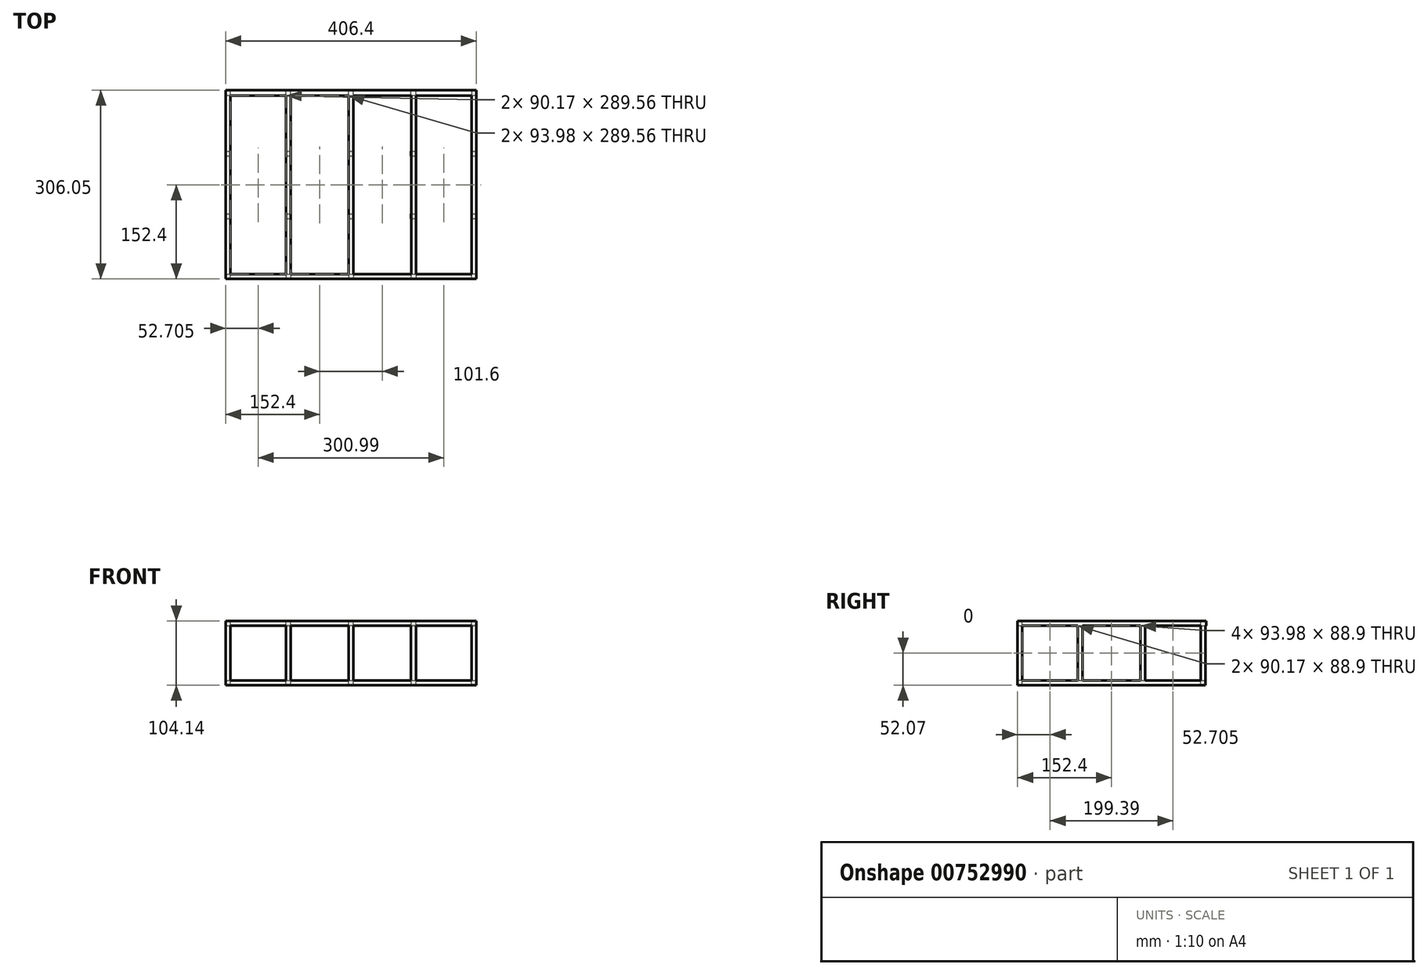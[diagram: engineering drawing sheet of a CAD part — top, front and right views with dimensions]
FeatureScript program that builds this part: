
annotation { "Feature Type Name" : "Feature", "Feature Type Description" : "" }
export const myFeature = defineFeature(function(context is Context, id is Id, definition is map)
    precondition{}
    {
        {
            var Q0;
            Q0=qCreatedBy(makeId("Top.planeOp"),FACE);
            var sketch = newSketch(context, id + "F0", { "sketchPlane" : qUnion([Q0])});
            skLineSegment(sketch, "E0.bottom", {"start": v(0, 0) * mm, "end": v(-406.4, 0) * mm});
            skLineSegment(sketch, "E0.top", {"start": v(0, 304.8) * mm, "end": v(-406.4, 304.8) * mm});
            skLineSegment(sketch, "E0.left", {"start": v(0, 0) * mm, "end": v(0, 304.8) * mm});
            skLineSegment(sketch, "E0.right", {"start": v(-406.4, 0) * mm, "end": v(-406.4, 304.8) * mm});
            skSolve(sketch);
        }
        {
            var Q0;
            Q0 = qSketchRegion(id + "F0", true);
            extrude(context, id + "F1", {"entities" : qUnion([Q0]), "depth" : 7.62 * mm, "offsetDistance" : 25.4 * mm});
        }
        {
            var Q0;
            Q0=makeQuery(id+"F1.opExtrude","CAP_FACE",FACE,{"disambiguationData":[OSD([sQuery(id+"F0.wireOp",EDGE,"E0.bottom"),sQuery(id+"F0.wireOp",EDGE,"E0.top"),sQuery(id+"F0.wireOp",EDGE,"E0.left"),sQuery(id+"F0.wireOp",EDGE,"E0.right")])],"isStart":false});
            var sketch = newSketch(context, id + "F2", { "sketchPlane" : qUnion([Q0])});
            skLineSegment(sketch, "E1", {"start": v(-406.4, 0) * mm, "end": v(-398.78, 0) * mm});
            skLineSegment(sketch, "E2", {"start": v(-398.78, 0) * mm, "end": v(-308.61, 0) * mm});
            skLineSegment(sketch, "E3", {"start": v(-308.61, 0) * mm, "end": v(-301, 0) * mm});
            skLineSegment(sketch, "E4", {"start": v(-105.41, 0) * mm, "end": v(-97.8, 0) * mm});
            skLineSegment(sketch, "E5", {"start": v(-97.8, 0) * mm, "end": v(-7.62, 0) * mm});
            skLineSegment(sketch, "E6", {"start": v(-7.62, 0) * mm, "end": v(-7.62, 7.62) * mm});
            skLineSegment(sketch, "E7", {"start": v(-406.4, 0) * mm, "end": v(-406.4, 297.18) * mm});
            skLineSegment(sketch, "E8.bottom", {"start": v(-7.62, 7.62) * mm, "end": v(-97.8, 7.62) * mm});
            skLineSegment(sketch, "E8.top", {"start": v(-7.62, 297.18) * mm, "end": v(-97.8, 297.18) * mm});
            skLineSegment(sketch, "E8.left", {"start": v(-7.62, 7.62) * mm, "end": v(-7.62, 297.18) * mm});
            skLineSegment(sketch, "E8.right", {"start": v(-97.8, 7.62) * mm, "end": v(-97.8, 297.18) * mm});
            skLineSegment(sketch, "E9.bottom", {"start": v(-398.78, 7.62) * mm, "end": v(-308.61, 7.62) * mm});
            skLineSegment(sketch, "E9.top", {"start": v(-398.78, 297.18) * mm, "end": v(-308.61, 297.18) * mm});
            skLineSegment(sketch, "E9.left", {"start": v(-398.78, 7.62) * mm, "end": v(-398.78, 297.18) * mm});
            skLineSegment(sketch, "E9.right", {"start": v(-308.61, 7.62) * mm, "end": v(-308.61, 297.18) * mm});
            skLineSegment(sketch, "E10", {"start": v(-105.41, 0) * mm, "end": v(-199.4, 0) * mm});
            skLineSegment(sketch, "E11", {"start": v(-199.4, 0) * mm, "end": v(-207.01, 0) * mm});
            skLineSegment(sketch, "E12", {"start": v(-207.01, 0) * mm, "end": v(-301, 0) * mm});
            skLineSegment(sketch, "E13.bottom", {"start": v(-301, 7.62) * mm, "end": v(-207.01, 7.62) * mm});
            skLineSegment(sketch, "E13.top", {"start": v(-301, 297.18) * mm, "end": v(-207.01, 297.18) * mm});
            skLineSegment(sketch, "E13.left", {"start": v(-301, 7.62) * mm, "end": v(-301, 297.18) * mm});
            skLineSegment(sketch, "E13.right", {"start": v(-207.01, 7.62) * mm, "end": v(-207.01, 297.18) * mm});
            skLineSegment(sketch, "E14.bottom", {"start": v(-199.4, 7.62) * mm, "end": v(-105.41, 7.62) * mm});
            skLineSegment(sketch, "E14.top", {"start": v(-199.4, 297.18) * mm, "end": v(-105.41, 297.18) * mm});
            skLineSegment(sketch, "E14.left", {"start": v(-199.4, 7.62) * mm, "end": v(-199.4, 297.18) * mm});
            skLineSegment(sketch, "E14.right", {"start": v(-105.41, 7.62) * mm, "end": v(-105.41, 297.18) * mm});
            skSolve(sketch);
        }
        {
            var Q0;
            Q0 = qSketchRegion(id + "F2", true);
            extrude(context, id + "F3", {"entities" : qUnion([Q0]), "operationType" : NewBodyOperationType.REMOVE, "oppositeDirection" : true, "depth" : 7.62 * mm, "offsetDistance" : 25.4 * mm});
        }
        {
            var Q0;
            Q0=makeQuery(id+"F1.opExtrude","CAP_FACE",FACE,{"disambiguationData":[OSD([sQuery(id+"F0.wireOp",EDGE,"E0.bottom"),sQuery(id+"F0.wireOp",EDGE,"E0.top"),sQuery(id+"F0.wireOp",EDGE,"E0.left"),sQuery(id+"F0.wireOp",EDGE,"E0.right")])],"isStart":false});
            var sketch = newSketch(context, id + "F4", { "sketchPlane" : qUnion([Q0])});
            skLineSegment(sketch, "E15.bottom", {"start": v(-406.4, 0) * mm, "end": v(-398.78, 0) * mm});
            skLineSegment(sketch, "E15.top", {"start": v(-406.4, 7.62) * mm, "end": v(-398.78, 7.62) * mm});
            skLineSegment(sketch, "E15.left", {"start": v(-406.4, 0) * mm, "end": v(-406.4, 7.62) * mm});
            skLineSegment(sketch, "E15.right", {"start": v(-398.78, 0) * mm, "end": v(-398.78, 7.62) * mm});
            skLineSegment(sketch, "E16.bottom", {"start": v(-308.61, 7.62) * mm, "end": v(-300.99, 7.62) * mm});
            skLineSegment(sketch, "E16.top", {"start": v(-308.61, 0) * mm, "end": v(-300.99, 0) * mm});
            skLineSegment(sketch, "E16.left", {"start": v(-308.61, 7.62) * mm, "end": v(-308.61, 0) * mm});
            skLineSegment(sketch, "E16.right", {"start": v(-300.99, 7.62) * mm, "end": v(-300.99, 0) * mm});
            skLineSegment(sketch, "E17.bottom", {"start": v(-105.74, 7.62) * mm, "end": v(-97.8, 7.62) * mm});
            skLineSegment(sketch, "E17.top", {"start": v(-105.74, 0) * mm, "end": v(-97.8, 0) * mm});
            skLineSegment(sketch, "E17.left", {"start": v(-105.74, 7.62) * mm, "end": v(-105.74, 0) * mm});
            skLineSegment(sketch, "E17.right", {"start": v(-97.8, 7.62) * mm, "end": v(-97.8, 0) * mm});
            skLineSegment(sketch, "E18.bottom", {"start": v(0, 0) * mm, "end": v(-7.62, 0) * mm});
            skLineSegment(sketch, "E18.top", {"start": v(0, 7.62) * mm, "end": v(-7.62, 7.62) * mm});
            skLineSegment(sketch, "E18.left", {"start": v(0, 0) * mm, "end": v(0, 7.62) * mm});
            skLineSegment(sketch, "E18.right", {"start": v(-7.62, 0) * mm, "end": v(-7.62, 7.62) * mm});
            skLineSegment(sketch, "E19.bottom", {"start": v(0, 304.8) * mm, "end": v(-7.62, 304.8) * mm});
            skLineSegment(sketch, "E19.top", {"start": v(0, 297.18) * mm, "end": v(-7.62, 297.18) * mm});
            skLineSegment(sketch, "E19.left", {"start": v(0, 304.8) * mm, "end": v(0, 297.18) * mm});
            skLineSegment(sketch, "E19.right", {"start": v(-7.62, 304.8) * mm, "end": v(-7.62, 297.18) * mm});
            skLineSegment(sketch, "E20.bottom", {"start": v(-97.8, 297.18) * mm, "end": v(-105.74, 297.18) * mm});
            skLineSegment(sketch, "E20.top", {"start": v(-97.8, 304.8) * mm, "end": v(-105.74, 304.8) * mm});
            skLineSegment(sketch, "E20.left", {"start": v(-97.8, 297.18) * mm, "end": v(-97.8, 304.8) * mm});
            skLineSegment(sketch, "E20.right", {"start": v(-105.74, 297.18) * mm, "end": v(-105.74, 304.8) * mm});
            skLineSegment(sketch, "E21.bottom", {"start": v(-301, 297.18) * mm, "end": v(-308.61, 297.18) * mm});
            skLineSegment(sketch, "E21.top", {"start": v(-301, 304.8) * mm, "end": v(-308.61, 304.8) * mm});
            skLineSegment(sketch, "E21.left", {"start": v(-301, 297.18) * mm, "end": v(-301, 304.8) * mm});
            skLineSegment(sketch, "E21.right", {"start": v(-308.61, 297.18) * mm, "end": v(-308.61, 304.8) * mm});
            skLineSegment(sketch, "E22.bottom", {"start": v(-398.78, 297.18) * mm, "end": v(-406.4, 297.18) * mm});
            skLineSegment(sketch, "E22.top", {"start": v(-398.78, 304.8) * mm, "end": v(-406.4, 304.8) * mm});
            skLineSegment(sketch, "E22.left", {"start": v(-398.78, 297.18) * mm, "end": v(-398.78, 304.8) * mm});
            skLineSegment(sketch, "E22.right", {"start": v(-406.4, 297.18) * mm, "end": v(-406.4, 304.8) * mm});
            skLineSegment(sketch, "E23", {"start": v(-406.4, 7.62) * mm, "end": v(-406.4, 97.8) * mm});
            skLineSegment(sketch, "E24", {"start": v(-406.4, 97.8) * mm, "end": v(-406.4, 105.4) * mm});
            skLineSegment(sketch, "E25", {"start": v(-406.4, 105.4) * mm, "end": v(-406.4, 162.15) * mm});
            skLineSegment(sketch, "E26", {"start": v(-406.4, 105.4) * mm, "end": v(-406.4, 199.4) * mm});
            skLineSegment(sketch, "E27", {"start": v(-406.4, 199.4) * mm, "end": v(-406.4, 281.57) * mm});
            skLineSegment(sketch, "E28", {"start": v(-406.4, 199.4) * mm, "end": v(-406.4, 207) * mm});
            skLineSegment(sketch, "E29", {"start": v(-406.4, 207) * mm, "end": v(-406.4, 297.18) * mm});
            skLineSegment(sketch, "E30.bottom", {"start": v(-406.4, 207) * mm, "end": v(-398.78, 207) * mm});
            skLineSegment(sketch, "E30.top", {"start": v(-406.4, 199.4) * mm, "end": v(-398.78, 199.4) * mm});
            skLineSegment(sketch, "E30.left", {"start": v(-406.4, 207) * mm, "end": v(-406.4, 199.4) * mm});
            skLineSegment(sketch, "E30.right", {"start": v(-398.78, 207) * mm, "end": v(-398.78, 199.4) * mm});
            skLineSegment(sketch, "E31.bottom", {"start": v(-406.4, 105.4) * mm, "end": v(-398.78, 105.4) * mm});
            skLineSegment(sketch, "E31.top", {"start": v(-406.4, 97.8) * mm, "end": v(-398.78, 97.8) * mm});
            skLineSegment(sketch, "E31.left", {"start": v(-406.4, 105.4) * mm, "end": v(-406.4, 97.8) * mm});
            skLineSegment(sketch, "E31.right", {"start": v(-398.78, 105.4) * mm, "end": v(-398.78, 97.8) * mm});
            skLineSegment(sketch, "E32.bottom", {"start": v(-308.61, 97.8) * mm, "end": v(-301, 97.8) * mm});
            skLineSegment(sketch, "E32.top", {"start": v(-308.61, 105.4) * mm, "end": v(-301, 105.4) * mm});
            skLineSegment(sketch, "E32.left", {"start": v(-308.61, 97.8) * mm, "end": v(-308.61, 105.4) * mm});
            skLineSegment(sketch, "E32.right", {"start": v(-301, 97.8) * mm, "end": v(-301, 105.4) * mm});
            skLineSegment(sketch, "E33.bottom", {"start": v(-308.61, 199.4) * mm, "end": v(-301, 199.4) * mm});
            skLineSegment(sketch, "E33.top", {"start": v(-308.61, 207) * mm, "end": v(-301, 207) * mm});
            skLineSegment(sketch, "E33.left", {"start": v(-308.61, 199.4) * mm, "end": v(-308.61, 207) * mm});
            skLineSegment(sketch, "E33.right", {"start": v(-301, 199.4) * mm, "end": v(-301, 207) * mm});
            skLineSegment(sketch, "E34.bottom", {"start": v(-105.74, 97.8) * mm, "end": v(-97.8, 97.8) * mm});
            skLineSegment(sketch, "E34.top", {"start": v(-105.74, 105.4) * mm, "end": v(-97.8, 105.4) * mm});
            skLineSegment(sketch, "E34.left", {"start": v(-105.74, 97.8) * mm, "end": v(-105.74, 105.4) * mm});
            skLineSegment(sketch, "E34.right", {"start": v(-97.8, 97.8) * mm, "end": v(-97.8, 105.4) * mm});
            skLineSegment(sketch, "E35.bottom", {"start": v(-105.74, 207) * mm, "end": v(-97.8, 207) * mm});
            skLineSegment(sketch, "E35.top", {"start": v(-105.74, 199.4) * mm, "end": v(-97.8, 199.4) * mm});
            skLineSegment(sketch, "E35.left", {"start": v(-105.74, 207) * mm, "end": v(-105.74, 199.4) * mm});
            skLineSegment(sketch, "E35.right", {"start": v(-97.8, 207) * mm, "end": v(-97.8, 199.4) * mm});
            skLineSegment(sketch, "E36.bottom", {"start": v(-7.62, 207) * mm, "end": v(0, 207) * mm});
            skLineSegment(sketch, "E36.top", {"start": v(-7.62, 199.4) * mm, "end": v(0, 199.4) * mm});
            skLineSegment(sketch, "E36.left", {"start": v(-7.62, 207) * mm, "end": v(-7.62, 199.4) * mm});
            skLineSegment(sketch, "E36.right", {"start": v(0, 207) * mm, "end": v(0, 199.4) * mm});
            skPoint(sketch, "E37.oppositeSnap0", {"position": v(-203.2, 0) * mm});
            skLineSegment(sketch, "E37.bottom", {"start": v(-207.01, 7.62) * mm, "end": v(-199.4, 7.62) * mm});
            skLineSegment(sketch, "E37.top", {"start": v(-207.01, 0) * mm, "end": v(-199.4, 0) * mm});
            skLineSegment(sketch, "E37.left", {"start": v(-207.01, 7.62) * mm, "end": v(-207.01, 0) * mm});
            skLineSegment(sketch, "E37.right", {"start": v(-199.4, 7.62) * mm, "end": v(-199.4, 0) * mm});
            skLineSegment(sketch, "E38.bottom", {"start": v(-207.01, 105.4) * mm, "end": v(-199.4, 105.4) * mm});
            skLineSegment(sketch, "E38.top", {"start": v(-207.01, 97.8) * mm, "end": v(-199.4, 97.8) * mm});
            skLineSegment(sketch, "E38.left", {"start": v(-207.01, 105.4) * mm, "end": v(-207.01, 97.8) * mm});
            skLineSegment(sketch, "E38.right", {"start": v(-199.4, 105.4) * mm, "end": v(-199.4, 97.8) * mm});
            skLineSegment(sketch, "E39.bottom", {"start": v(-207.01, 199.4) * mm, "end": v(-199.4, 199.4) * mm});
            skLineSegment(sketch, "E39.top", {"start": v(-207.01, 207) * mm, "end": v(-199.4, 207) * mm});
            skLineSegment(sketch, "E39.left", {"start": v(-207.01, 199.4) * mm, "end": v(-207.01, 207) * mm});
            skLineSegment(sketch, "E39.right", {"start": v(-199.4, 199.4) * mm, "end": v(-199.4, 207) * mm});
            skPoint(sketch, "E40.oppositeSnap0", {"position": v(-203.2, 304.8) * mm});
            skLineSegment(sketch, "E40.bottom", {"start": v(-207.01, 297.18) * mm, "end": v(-199.4, 297.18) * mm});
            skLineSegment(sketch, "E40.top", {"start": v(-207.01, 304.8) * mm, "end": v(-199.4, 304.8) * mm});
            skLineSegment(sketch, "E40.left", {"start": v(-207.01, 297.18) * mm, "end": v(-207.01, 304.8) * mm});
            skLineSegment(sketch, "E40.right", {"start": v(-199.4, 297.18) * mm, "end": v(-199.4, 304.8) * mm});
            skLineSegment(sketch, "E41.bottom", {"start": v(-7.62, 97.8) * mm, "end": v(0, 97.8) * mm});
            skLineSegment(sketch, "E41.top", {"start": v(-7.62, 105.4) * mm, "end": v(0, 105.4) * mm});
            skLineSegment(sketch, "E41.left", {"start": v(-7.62, 97.8) * mm, "end": v(-7.62, 105.4) * mm});
            skLineSegment(sketch, "E41.right", {"start": v(0, 97.8) * mm, "end": v(0, 105.4) * mm});
            skSolve(sketch);
        }
        {
            var Q0;
            Q0 = qSketchRegion(id + "F4", true);
            extrude(context, id + "F5", {"entities" : qUnion([Q0]), "operationType" : NewBodyOperationType.ADD, "depth" : 88.9 * mm, "offsetDistance" : 25.4 * mm});
        }
        {
            var Q0;
            Q0=makeQuery(id+"F5.opExtrude","CAP_FACE",FACE,{"disambiguationData":[OSD([sQuery(id+"F4.wireOp",EDGE,"E15.bottom"),sQuery(id+"F4.wireOp",EDGE,"E15.top"),sQuery(id+"F4.wireOp",EDGE,"E15.left"),sQuery(id+"F4.wireOp",EDGE,"E15.right")])],"isStart":false});
            var sketch = newSketch(context, id + "F6", { "sketchPlane" : qUnion([Q0])});
            skLineSegment(sketch, "E42.bottom", {"start": v(-406.4, 0) * mm, "end": v(0, 0) * mm});
            skLineSegment(sketch, "E42.top", {"start": v(-406.4, 306.05) * mm, "end": v(0, 306.05) * mm});
            skLineSegment(sketch, "E42.left", {"start": v(-406.4, 0) * mm, "end": v(-406.4, 306.05) * mm});
            skLineSegment(sketch, "E42.right", {"start": v(0, 0) * mm, "end": v(0, 306.05) * mm});
            skSolve(sketch);
        }
        {
            var Q0;
            Q0 = qSketchRegion(id + "F6", true);
            extrude(context, id + "F7", {"entities" : qUnion([Q0]), "operationType" : NewBodyOperationType.ADD, "depth" : 7.62 * mm, "offsetDistance" : 25.4 * mm});
        }
        {
            var Q0;
            Q0=makeQuery(id+"F7.opExtrude","CAP_FACE",FACE,{"disambiguationData":[OSD([sQuery(id+"F6.wireOp",EDGE,"E42.bottom"),sQuery(id+"F6.wireOp",EDGE,"E42.top"),sQuery(id+"F6.wireOp",EDGE,"E42.left"),sQuery(id+"F6.wireOp",EDGE,"E42.right")])],"isStart":false});
            var sketch = newSketch(context, id + "F8", { "sketchPlane" : qUnion([Q0])});
            skLineSegment(sketch, "E43", {"start": v(-406.4, 0) * mm, "end": v(-406.4, 7.62) * mm});
            skLineSegment(sketch, "E44", {"start": v(-406.4, 7.62) * mm, "end": v(-406.4, 0) * mm});
            skLineSegment(sketch, "E45", {"start": v(-406.4, 0) * mm, "end": v(-398.78, 0) * mm});
            skLineSegment(sketch, "E46", {"start": v(-398.78, 0) * mm, "end": v(-308.61, 0) * mm});
            skLineSegment(sketch, "E47", {"start": v(-308.61, 0) * mm, "end": v(-301, 0) * mm});
            skLineSegment(sketch, "E48", {"start": v(-301, 0) * mm, "end": v(-207.01, 0) * mm});
            skLineSegment(sketch, "E49", {"start": v(-207.01, 0) * mm, "end": v(-199.4, 0) * mm});
            skLineSegment(sketch, "E50", {"start": v(-199.4, 0) * mm, "end": v(-105.41, 0) * mm});
            skLineSegment(sketch, "E51", {"start": v(-105.41, 0) * mm, "end": v(-97.8, 0) * mm});
            skLineSegment(sketch, "E52", {"start": v(-97.8, 0) * mm, "end": v(-7.62, 0) * mm});
            skLineSegment(sketch, "E53", {"start": v(-7.62, 0) * mm, "end": v(0, 0) * mm});
            skLineSegment(sketch, "E54.bottom", {"start": v(-398.78, 7.62) * mm, "end": v(-308.61, 7.62) * mm});
            skLineSegment(sketch, "E54.top", {"start": v(-398.78, 297.18) * mm, "end": v(-308.61, 297.18) * mm});
            skLineSegment(sketch, "E54.left", {"start": v(-398.78, 7.62) * mm, "end": v(-398.78, 297.18) * mm});
            skLineSegment(sketch, "E54.right", {"start": v(-308.61, 7.62) * mm, "end": v(-308.61, 297.18) * mm});
            skLineSegment(sketch, "E55.bottom", {"start": v(-301, 7.62) * mm, "end": v(-207.01, 7.62) * mm});
            skLineSegment(sketch, "E55.top", {"start": v(-301, 297.18) * mm, "end": v(-207.01, 297.18) * mm});
            skLineSegment(sketch, "E55.left", {"start": v(-301, 7.62) * mm, "end": v(-301, 297.18) * mm});
            skLineSegment(sketch, "E55.right", {"start": v(-207.01, 7.62) * mm, "end": v(-207.01, 297.18) * mm});
            skLineSegment(sketch, "E56.bottom", {"start": v(-199.4, 7.62) * mm, "end": v(-105.41, 7.62) * mm});
            skLineSegment(sketch, "E56.top", {"start": v(-199.4, 297.18) * mm, "end": v(-105.41, 297.18) * mm});
            skLineSegment(sketch, "E56.left", {"start": v(-199.4, 7.62) * mm, "end": v(-199.4, 297.18) * mm});
            skLineSegment(sketch, "E56.right", {"start": v(-105.41, 7.62) * mm, "end": v(-105.41, 297.18) * mm});
            skLineSegment(sketch, "E57.bottom", {"start": v(-97.8, 7.62) * mm, "end": v(-7.62, 7.62) * mm});
            skLineSegment(sketch, "E57.top", {"start": v(-97.8, 297.18) * mm, "end": v(-7.62, 297.18) * mm});
            skLineSegment(sketch, "E57.left", {"start": v(-97.8, 7.62) * mm, "end": v(-97.8, 297.18) * mm});
            skLineSegment(sketch, "E57.right", {"start": v(-7.62, 7.62) * mm, "end": v(-7.62, 297.18) * mm});
            skSolve(sketch);
        }
        {
            var Q0;
            Q0 = qSketchRegion(id + "F8", true);
            extrude(context, id + "F9", {"entities" : qUnion([Q0]), "operationType" : NewBodyOperationType.REMOVE, "oppositeDirection" : true, "depth" : 7.62 * mm, "offsetDistance" : 25.4 * mm});
        }
    });
